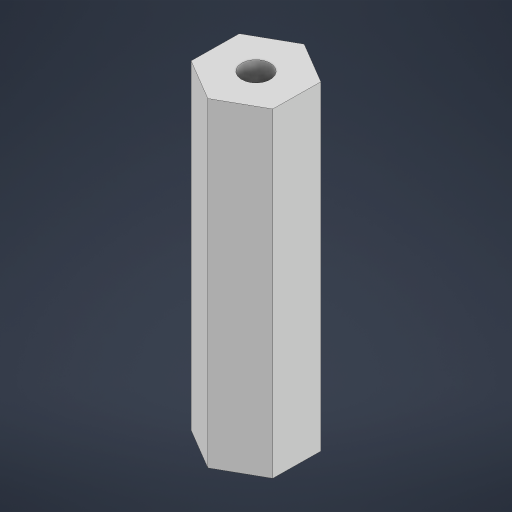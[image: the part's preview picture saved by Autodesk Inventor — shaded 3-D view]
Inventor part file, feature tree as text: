
AUTODESK INVENTOR PART (.ipt)
format: ipt  version: 2024.3 (Build 283343000, 343)  size: 162,304 bytes
history: native  units: in
note: dims shown in document units (in); Inventor stores cm internally (conversion verified against a paired STEP export)
features: extrude x1, sketch x1
ambient origin geometry x8: Origin, YZ Plane, XZ Plane, XY Plane, X Axis, Y Axis, Z Axis, Center Point
bodies: Solid1 (feature_tree)
feature tree (2):
  extrude  "Extrusion1"  Depth=1.78in TaperAngle=0.0deg
  sketch  "Sketch1"  dims[d0=0.159in d1=1.78in d2=0.0in]
